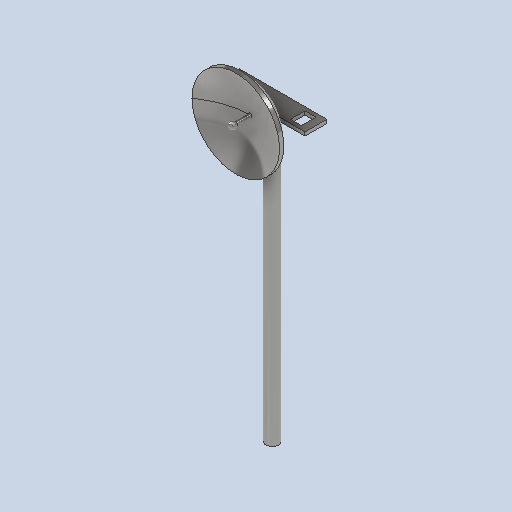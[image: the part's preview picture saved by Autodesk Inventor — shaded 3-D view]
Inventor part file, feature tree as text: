
AUTODESK INVENTOR PART (.ipt)
format: ipt  version: 2024 (Build 280153000, 153)  size: 183,296 bytes
history: native  units: in
note: dims shown in document units (in); Inventor stores cm internally (conversion verified against a paired STEP export)
features: other x8, plane x2
ambient origin geometry x8: Origin, YZ Plane, XZ Plane, XY Plane, X Axis, Y Axis, Z Axis, Center Point
bodies: Solid1 (feature_tree)
feature tree (10):
  other  "hubble_antenna.ipt"
  other  "Solid1::hubble_antenna.ipt"
  other  "TaggingFeature1"
  other  "pole_sketch"
  other  "dish_support_sketch"
  other  "dish_sketch"
  other  "interior_antenna_sketch"
  other  "slot_sketch"
  plane  "Work Plane1"
  plane  "Work Plane2"
